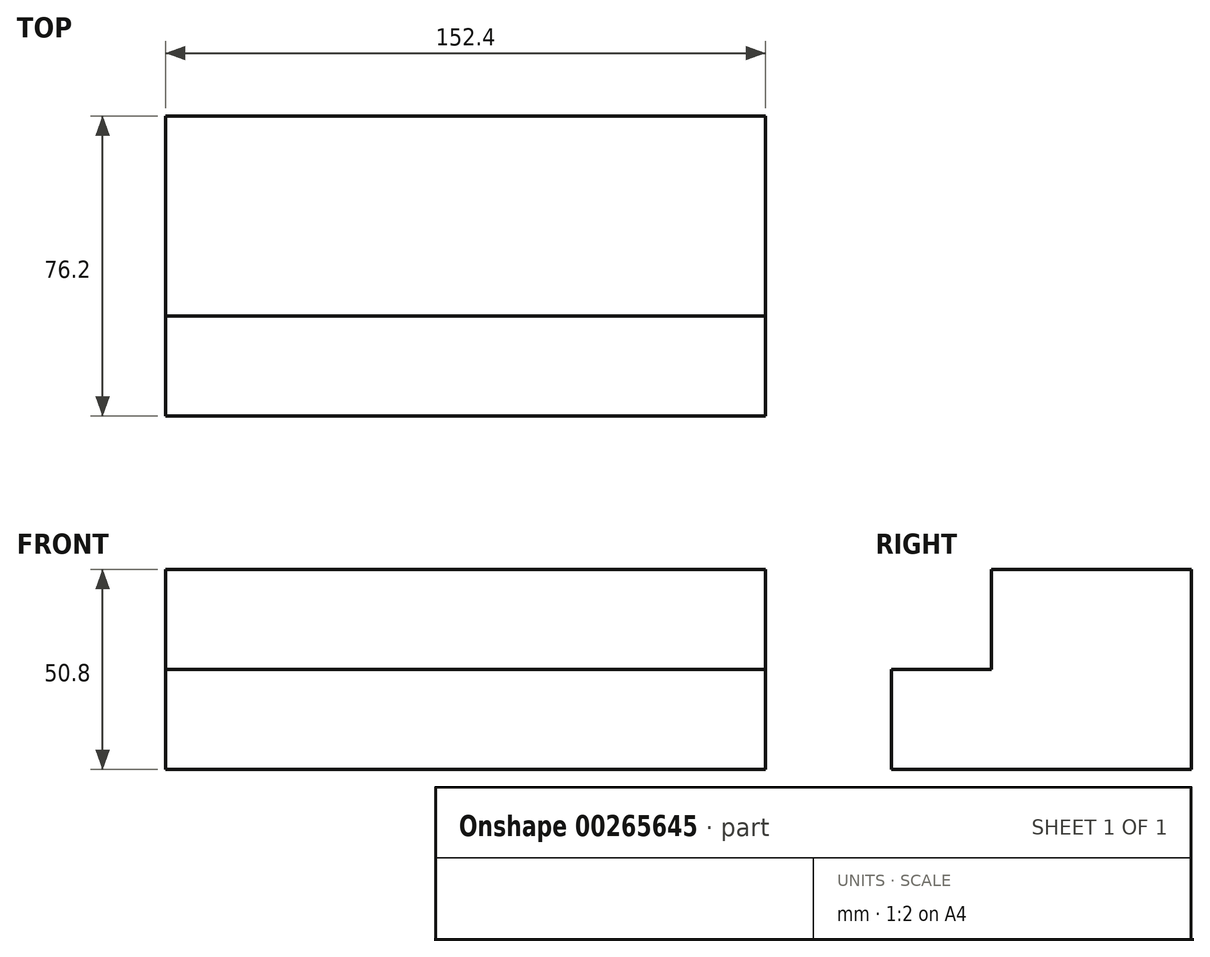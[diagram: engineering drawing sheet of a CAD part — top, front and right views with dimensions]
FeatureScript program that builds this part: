
annotation { "Feature Type Name" : "Feature", "Feature Type Description" : "" }
export const myFeature = defineFeature(function(context is Context, id is Id, definition is map)
    precondition{}
    {
        {
            var Q0;
            Q0=qCreatedBy(makeId("Right.planeOp"),FACE);
            var sketch = newSketch(context, id + "F0", { "sketchPlane" : qUnion([Q0])});
            skLineSegment(sketch, "E0", {"start": v(0, 0) * mm, "end": v(76.2, 0) * mm});
            skLineSegment(sketch, "E1", {"start": v(76.2, 0) * mm, "end": v(76.2, 50.8) * mm});
            skLineSegment(sketch, "E2", {"start": v(0, 0) * mm, "end": v(0, 25.4) * mm});
            skLineSegment(sketch, "E3", {"start": v(0, 25.4) * mm, "end": v(25.4, 25.4) * mm});
            skLineSegment(sketch, "E4", {"start": v(25.4, 25.4) * mm, "end": v(25.4, 50.8) * mm});
            skLineSegment(sketch, "E5", {"start": v(25.4, 50.8) * mm, "end": v(76.2, 50.8) * mm});
            skSolve(sketch);
        }
        {
            var Q0;
            Q0 = qSketchRegion(id + "F0", true);
            extrude(context, id + "F1", {"entities" : qUnion([Q0]), "depth" : 152.4 * mm});
        }
    });
